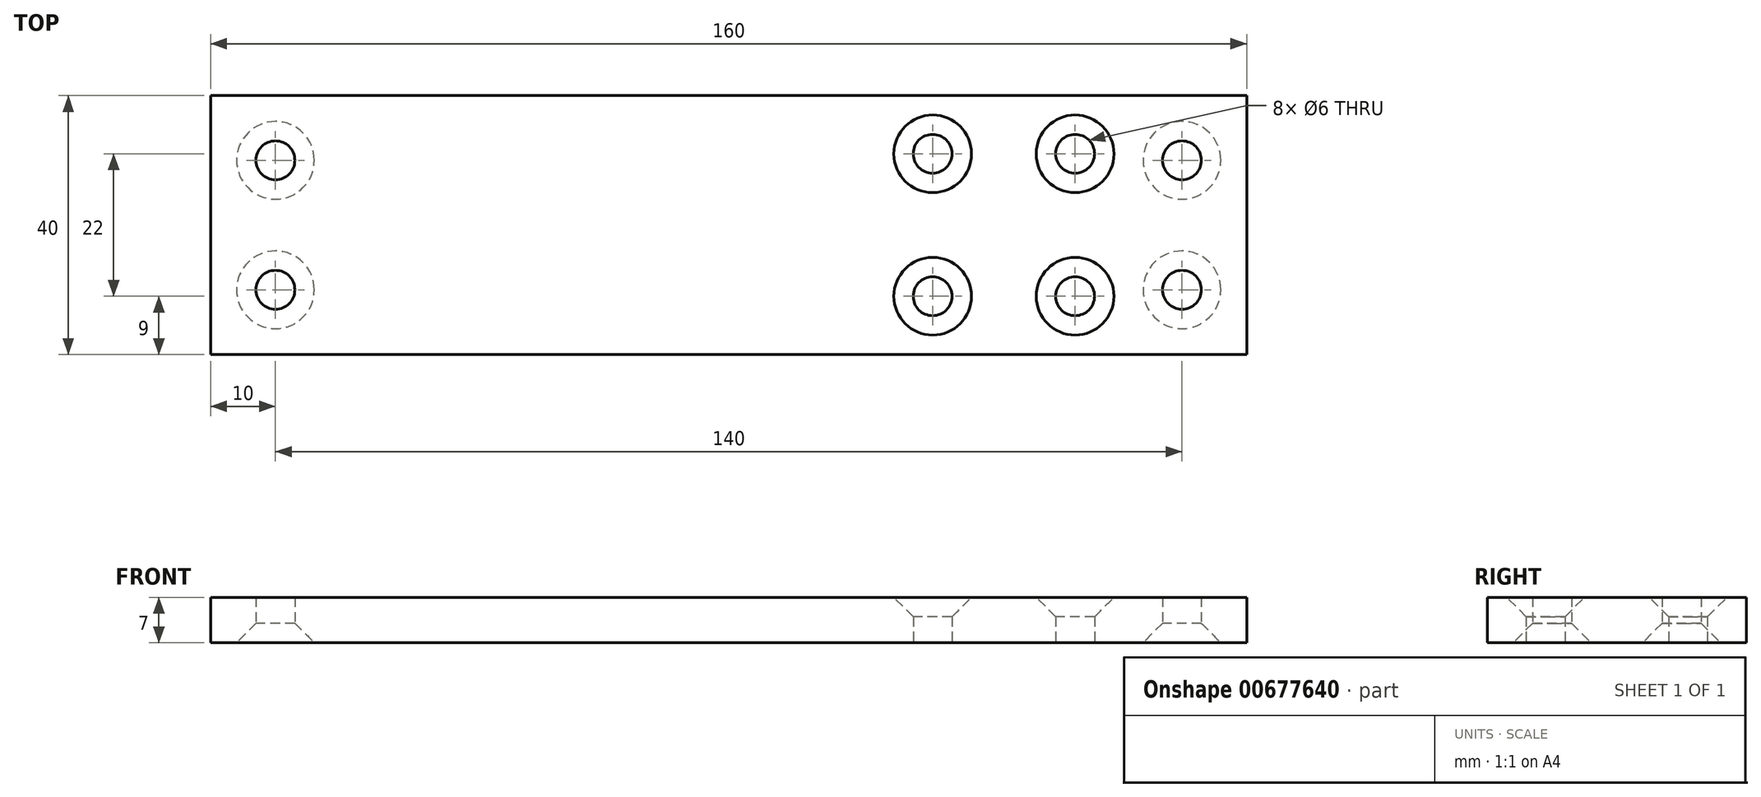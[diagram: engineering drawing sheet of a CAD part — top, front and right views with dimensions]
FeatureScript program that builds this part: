
annotation { "Feature Type Name" : "Feature", "Feature Type Description" : "" }
export const myFeature = defineFeature(function(context is Context, id is Id, definition is map)
    precondition{}
    {
        {
            var Q0;
            Q0=qCreatedBy(makeId("Top.planeOp"),FACE);
            var sketch = newSketch(context, id + "F0", { "sketchPlane" : qUnion([Q0])});
            skLineSegment(sketch, "E0.bottom", {"start": v(0, 0) * mm, "end": v(160, 0) * mm});
            skLineSegment(sketch, "E0.top", {"start": v(0, 40) * mm, "end": v(160, 40) * mm});
            skLineSegment(sketch, "E0.left", {"start": v(0, 0) * mm, "end": v(0, 40) * mm});
            skLineSegment(sketch, "E0.right", {"start": v(160, 0) * mm, "end": v(160, 40) * mm});
            skCircle(sketch, "E1", {"center": v(133.5, 9) * mm, "radius": 3 * mm});
            skCircle(sketch, "E2.0.1.0", {"center": v(133.5, 31) * mm, "radius": 3 * mm});
            skCircle(sketch, "E2.1.0.0", {"center": v(111.5, 9) * mm, "radius": 3 * mm});
            skCircle(sketch, "E2.1.1.0", {"center": v(111.5, 31) * mm, "radius": 3 * mm});
            skLineSegment(sketch, "E2.direction1", {"start": v(133.5, 9) * mm, "end": v(111.5, 9) * mm, "construction": true});
            skLineSegment(sketch, "E2.direction2", {"start": v(133.5, 9) * mm, "end": v(133.5, 31) * mm, "construction": true});
            skCircle(sketch, "E3", {"center": v(150, 10) * mm, "radius": 3 * mm});
            skCircle(sketch, "E4.0.1.0", {"center": v(150, 30) * mm, "radius": 3 * mm});
            skLineSegment(sketch, "E4.direction1", {"start": v(150, 10) * mm, "end": v(175, 10) * mm, "construction": true});
            skLineSegment(sketch, "E4.direction2", {"start": v(150, 10) * mm, "end": v(150, 30) * mm, "construction": true});
            skCircle(sketch, "E5", {"center": v(10, 10) * mm, "radius": 3 * mm});
            skCircle(sketch, "E6.0.1.0", {"center": v(10, 30) * mm, "radius": 3 * mm});
            skLineSegment(sketch, "E6.direction1", {"start": v(10, 10) * mm, "end": v(35, 10) * mm, "construction": true});
            skLineSegment(sketch, "E6.direction2", {"start": v(10, 10) * mm, "end": v(10, 30) * mm, "construction": true});
            skSolve(sketch);
        }
        {
            var Q0;
            Q0=makeQuery(id+"F0.imprint","IMPRINT",FACE,{"disambiguationData":[TD([[makeQuery(id+"F0.imprint","IMPRINT",EDGE,{"derivedFrom":sQuery(id+"F0.wireOp",EDGE,"E0.bottom")}),1.0]])]});
            extrude(context, id + "F1", {"entities" : qUnion([Q0]), "depth" : 7 * mm, "offsetDistance" : 25 * mm});
        }
        {
            var Q0;
            Q0=makeQuery(id+"F1.opExtrude","CAP_EDGE",EDGE,{"disambiguationData":[OSD([sQuery(id+"F0.wireOp",EDGE,"E2.1.1.0")])],"isStart":false});
            var Q1;
            Q1=makeQuery(id+"F1.opExtrude","CAP_EDGE",EDGE,{"disambiguationData":[OSD([sQuery(id+"F0.wireOp",EDGE,"E2.0.1.0")])],"isStart":false});
            var Q2;
            Q2=makeQuery(id+"F1.opExtrude","CAP_EDGE",EDGE,{"disambiguationData":[OSD([sQuery(id+"F0.wireOp",EDGE,"E1")])],"isStart":false});
            var Q3;
            Q3=makeQuery(id+"F1.opExtrude","CAP_EDGE",EDGE,{"disambiguationData":[OSD([sQuery(id+"F0.wireOp",EDGE,"E2.1.0.0")])],"isStart":false});
            var Q4;
            Q4=makeQuery(id+"F1.opExtrude","CAP_EDGE",EDGE,{"disambiguationData":[OSD([sQuery(id+"F0.wireOp",EDGE,"E3")])],"isStart":true});
            var Q5;
            Q5=makeQuery(id+"F1.opExtrude","CAP_EDGE",EDGE,{"disambiguationData":[OSD([sQuery(id+"F0.wireOp",EDGE,"E4.0.1.0")])],"isStart":true});
            var Q6;
            Q6=makeQuery(id+"F1.opExtrude","CAP_EDGE",EDGE,{"disambiguationData":[OSD([sQuery(id+"F0.wireOp",EDGE,"E5")])],"isStart":true});
            var Q7;
            Q7=makeQuery(id+"F1.opExtrude","CAP_EDGE",EDGE,{"disambiguationData":[OSD([sQuery(id+"F0.wireOp",EDGE,"E6.0.1.0")])],"isStart":true});
            chamfer(context, id + "F2", {"entities" : qUnion([Q0, Q1, Q2, Q3, Q4, Q5, Q6, Q7]), "width" : 3 * mm, "tangentPropagation" : true});
        }
    });
